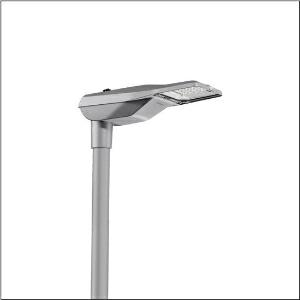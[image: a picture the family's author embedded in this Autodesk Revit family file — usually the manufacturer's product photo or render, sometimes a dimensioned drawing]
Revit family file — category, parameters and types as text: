
# Revit family: streetlight_sl_21_micro___st0_8a_5xe1c33s08db_f35f
name_source: partatom
category: Lighting Fixtures
units: mm (PartAtom-declared; Revit-internal decimal feet)

## family parameters
Cut with Voids When Loaded = No
Host = Face
Light Source = No
Part Type = Normal
Room Calculation Point = No
Round Connector Dimension = Use Diameter
Shared = No

## types (1)
- --- (1 x LED, 5110 lm, 39.1 W, 3000K)
    Apparent Load = 39 VA
    CIE Flux Codes = 38 75 97 100 100
    Color Rendering = 70
    Color Temperature = 3000K
    Default Elevation = 1800 mm
    Description = Streetlight SL 21 micro, mast luminaire, primary light control with lens, of PMMA, primary optical cover: cover, of toughened safety glass, transparent, light distribution: ST0.8a, light emission: direct distribution, primary light characteristic: asymmetric, installation type: side-entry, post-top, LED, High Power LED, rated luminous flux: 5.110lm, luminous efficacy: 131lm/W, light colour: 730, colour temperature: 3000K, control: flexible luminous flux parameterisation, time-dependent luminous flux control, constant luminous flux control, overheat protection, pre-setting: logarithmic dimming characteristic, mains connection: 220..240V, AC, 50/60Hz, start of lifetime: 39W, end of service life: 41W, reduction: 18W, luminaire housing, of diecast aluminium, powder-coated, Siteco® metallic grey (DB 702S), corrosivity category C5 mid according to DIN EN ISO 12944, please order mast flange separately, inclination adjustable: 0°, 5°, 10°, 15°, sealing non-destructively replaceable, multi-level sealing system, length: 528mm, width: 235mm, height: 110mm, mast flange for spigot size: 42mm (side-entry): 5XC10008XM4, 60/48mm (side-entry/post-top): 5XC10108XM2, 76/60mm (side-entry/post-top): 5XC10108XM1, Smart Interface above, protection rating (complete): IP66, insulation class (complete): insulation class II (safety insulation), certification: CE, ENEC, ENEC+, VDE, impact resistance: IK09, permissible operating ambient temperature for outdoor applications: -40..+50°C, standard-compliant lighting for roads and squares, packaging unit: 1 piece

Light Distribution: ST0.8a
    Height = 110 mm
    Lamp = 1 x LED
    Lamp Light Flux = 5110 lm
    Lamp Power = 39.1 W
    Lamp count = 1
    Length = 528 mm
    Luminous efficacy = 131 lm/W
    Manufacturer = Siteco
    ModVariant = No
    Model = 5XE1C33S08DB
    Number of Poles = 1
    OnlyDefault = Yes
    Power Factor = 1
    Product Name = Streetlight SL 21 micro | ST0.8a
    Product group = mast luminaire | pylon top
    ProductGroupID = 6100
    Protection Class = Protection class II
    Protection Degree = IP 66
    RLX_Detail_Level = 1
    RLX_Emergency_Light_Flux = 0 lm
    RLX_Emergency_Type = 0
    RLX_Emergency_Type_DB = No
    RlxData = <blob elided: 98861 chars, md5=2b0a39a9>
    Socket = socket
    Standby Power = 0 W
    System Light Flux = 5110 lm
    System Power = 39 W
    Type Comments = factory setting: luminous flux: 100 % | dim-lin: 254 | 765 mA
    Type Image = l_1277292.jpg
    URL = http://relux.com
    VarID = @adj_124799
    Voltage = 0 V
    Weight = 0.00 kg
    Width = 235 mm

## geometry (parser evidence)
native form markers: Blend x4, Sweep x10
no freeform markers — native parametric forms only
